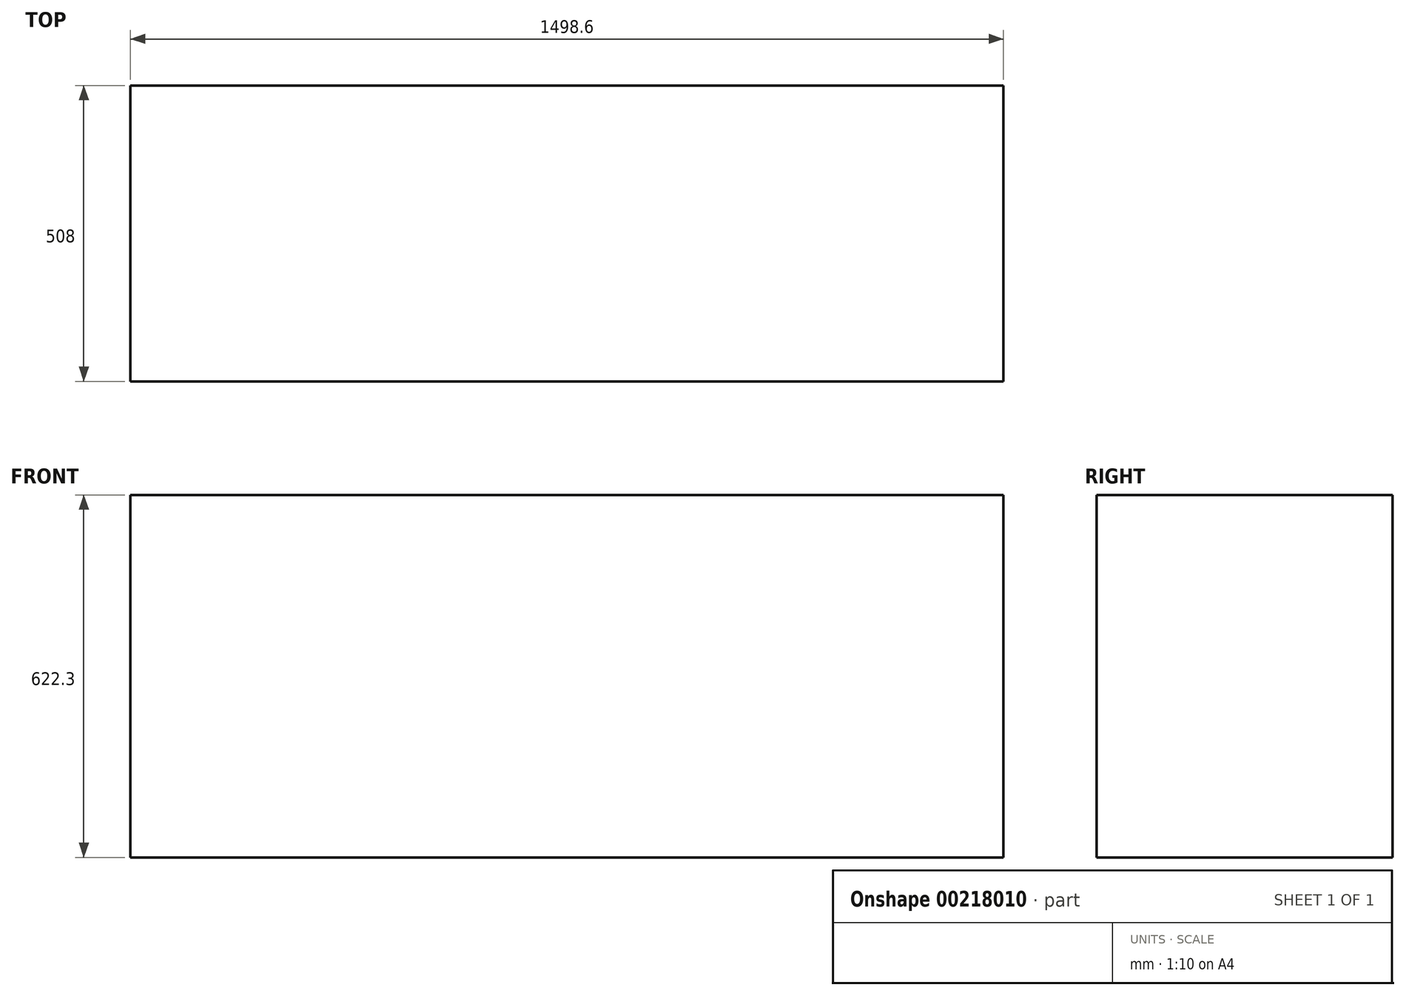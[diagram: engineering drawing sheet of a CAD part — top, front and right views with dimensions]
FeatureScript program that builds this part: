
annotation { "Feature Type Name" : "Feature", "Feature Type Description" : "" }
export const myFeature = defineFeature(function(context is Context, id is Id, definition is map)
    precondition{}
    {
        {
            var Q0;
            Q0=qCreatedBy(makeId("Top.planeOp"),FACE);
            var sketch = newSketch(context, id + "F0", { "sketchPlane" : qUnion([Q0])});
            skLineSegment(sketch, "E0.bottom", {"start": v(0, 0) * mm, "end": v(-1498.6, 0) * mm});
            skLineSegment(sketch, "E0.top", {"start": v(0, 508) * mm, "end": v(-1498.6, 508) * mm});
            skLineSegment(sketch, "E0.left", {"start": v(0, 0) * mm, "end": v(0, 508) * mm});
            skLineSegment(sketch, "E0.right", {"start": v(-1498.6, 0) * mm, "end": v(-1498.6, 508) * mm});
            skSolve(sketch);
        }
        {
            var Q0;
            Q0 = qSketchRegion(id + "F0", true);
            extrude(context, id + "F1", {"entities" : qUnion([Q0]), "depth" : 622.3 * mm});
        }
    });
